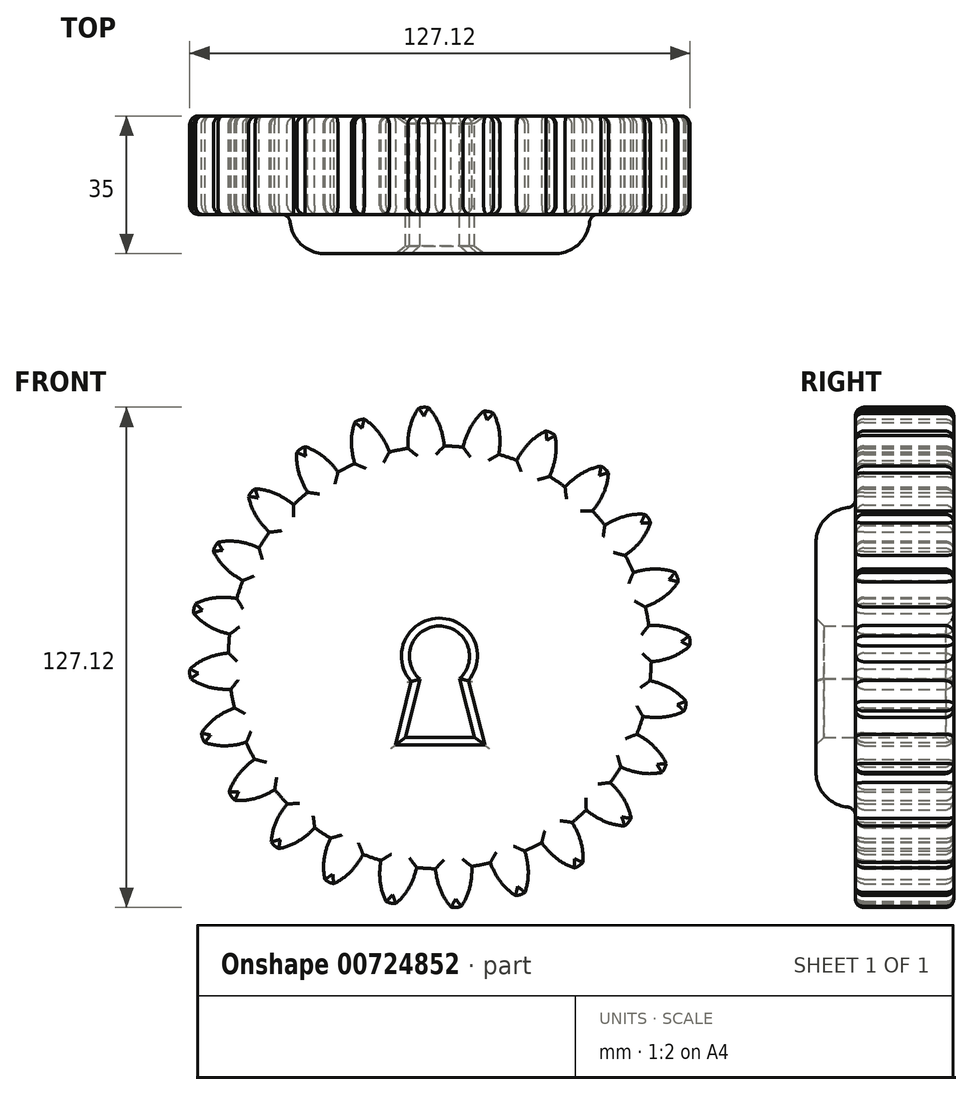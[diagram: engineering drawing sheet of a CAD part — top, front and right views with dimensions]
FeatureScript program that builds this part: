
annotation { "Feature Type Name" : "Feature", "Feature Type Description" : "" }
export const myFeature = defineFeature(function(context is Context, id is Id, definition is map)
    precondition{}
    {
        {
            var Q0;
            Q0=qCreatedBy(makeId("Front.planeOp"),FACE);
            var sketch = newSketch(context, id + "F0", { "sketchPlane" : qUnion([Q0])});
            skCircle(sketch, "E0", {"center": v(0, 0) * mm, "radius": 53.72 * mm});
            skCircle(sketch, "E1", {"center": v(0, 0) * mm, "radius": 58.67 * mm, "construction": true});
            skCircle(sketch, "E2", {"center": v(0, 0) * mm, "radius": 63.5 * mm, "construction": true});
            skLineSegment(sketch, "E3", {"start": v(0, 0) * mm, "end": v(0, 91.84) * mm, "construction": true});
            skLineSegment(sketch, "E4", {"start": v(0, 0) * mm, "end": v(-7.41, 113.09) * mm, "construction": true});
            skLineSegment(sketch, "E5", {"start": v(0, 58.67) * mm, "end": v(-83.5, 56.59) * mm, "construction": true});
            skLineSegment(sketch, "E6", {"start": v(0, 58.67) * mm, "end": v(-75.39, 29.08) * mm, "construction": true});
            skCircle(sketch, "E7", {"center": v(0, 0) * mm, "radius": 54.62 * mm, "construction": true});
            skCircle(sketch, "E8", {"center": v(0, 58.67) * mm, "radius": 16.52 * mm, "construction": true});
            skCircle(sketch, "E9", {"center": v(-15.38, 52.64) * mm, "radius": 16.52 * mm, "construction": true});
            skArc(sketch, "E10", {"start": v(0, 58.67) * mm, "mid": v(-1.21, 61.19) * mm, "end": v(-2.87, 63.43) * mm});
            skArc(sketch, "E11", {"start": v(1.1, 53.7) * mm, "mid": v(0.72, 56.23) * mm, "end": v(0, 58.67) * mm});
            skArc(sketch, "E12.MirrorCS", {"start": v(-8.1, 53.1) * mm, "mid": v(-8.06, 55.65) * mm, "end": v(-7.66, 58.17) * mm});
            skArc(sketch, "E13.MirrorCS", {"start": v(-7.66, 58.17) * mm, "mid": v(-6.78, 60.82) * mm, "end": v(-5.43, 63.27) * mm});
            skArc(sketch, "E14", {"start": v(-2.87, 63.43) * mm, "mid": v(-4.17, 63.55) * mm, "end": v(-5.43, 63.27) * mm});
            skCircle(sketch, "E15", {"center": v(-0.1, 0.31) * mm, "radius": 7.65 * mm});
            skLineSegment(sketch, "E16", {"start": v(-5.08, -5.5) * mm, "end": v(-8.74, -20.3) * mm});
            skLineSegment(sketch, "E17", {"start": v(-8.74, -20.3) * mm, "end": v(8.86, -20.3) * mm});
            skLineSegment(sketch, "E18", {"start": v(8.86, -20.3) * mm, "end": v(5.03, -5.36) * mm});
            skCircle(sketch, "E19", {"center": v(0, 0) * mm, "radius": 38.01 * mm});
            skSolve(sketch);
        }
        {
            var Q0;
            Q0=makeQuery(id+"F0.imprint","IMPRINT",FACE,{"disambiguationData":[TD([[makeQuery(id+"F0.imprint","IMPRINT",EDGE,{"derivedFrom":sQuery(id+"F0.wireOp",EDGE,"E19")}),-1.0]])]});
            var Q1;
            Q1=makeQuery(id+"F0.imprint","IMPRINT",FACE,{"disambiguationData":[TD([[makeQuery(id+"F0.imprint","IMPRINT",EDGE,{"derivedFrom":sQuery(id+"F0.wireOp",EDGE,"E10")}),1.0]])]});
            extrude(context, id + "F1", {"entities" : qUnion([Q0, Q1]), "depth" : 25 * mm, "offsetDistance" : 25 * mm});
        }
        {
            var Q0;
            Q0=makeQuery(id+"F1.opExtrude","SWEPT_BODY",BODY,{"disambiguationData":[OSD([sQuery(id+"F0.wireOp",EDGE,"E0"),sQuery(id+"F0.wireOp",EDGE,"E10"),sQuery(id+"F0.wireOp",EDGE,"E11"),sQuery(id+"F0.wireOp",EDGE,"E12.MirrorCS"),sQuery(id+"F0.wireOp",EDGE,"E13.MirrorCS"),sQuery(id+"F0.wireOp",EDGE,"E14")])]});
            var Q1;
            Q1=makeQuery(id+"F1.opExtrude","SWEPT_FACE",FACE,{"disambiguationData":[OSD([sQuery(id+"F0.wireOp",EDGE,"E0")])]});
            circularPattern(context, id + "F2", {"entities" : qUnion([Q0]), "axis" : qUnion([Q1]), "angle" : 360 * degree, "instanceCount" : 24, "equalSpace" : true});
        }
        {
            var Q0;
            {var subQ1=sQuery(id+"F0.wireOp",EDGE,"E16");Q0=makeQuery(id+"F0.imprint","IMPRINT",FACE,{"disambiguationData":[TD([[makeQuery(id+"F0.imprint","IMPRINT",EDGE,{"derivedFrom":subQ1}),-1.0]])]});}
            extrude(context, id + "F3", {"entities" : qUnion([Q0]), "operationType" : NewBodyOperationType.ADD, "depth" : 35 * mm, "offsetDistance" : 25 * mm});
        }
        {
            var Q0;
            {var subQ0=makeQuery(id+"F1.opExtrude","CAP_FACE",FACE,{"disambiguationData":[OSD([sQuery(id+"F0.wireOp",EDGE,"E0"),sQuery(id+"F0.wireOp",EDGE,"E10"),sQuery(id+"F0.wireOp",EDGE,"E11"),sQuery(id+"F0.wireOp",EDGE,"E12.MirrorCS"),sQuery(id+"F0.wireOp",EDGE,"E13.MirrorCS"),sQuery(id+"F0.wireOp",EDGE,"E14"),sQuery(id+"F0.wireOp",EDGE,"E19")])],"isStart":false});Q0=makeQuery(id+"F3.boolean.opBoolean","MERGE",FACE,{"derivedFrom":[subQ0,makeQuery(id+"F2.opPattern","COPY",FACE,{"derivedFrom":subQ0,"instanceName":"1"}),makeQuery(id+"F2.opPattern","COPY",FACE,{"derivedFrom":subQ0,"instanceName":"2"}),makeQuery(id+"F2.opPattern","COPY",FACE,{"derivedFrom":subQ0,"instanceName":"3"}),makeQuery(id+"F2.opPattern","COPY",FACE,{"derivedFrom":subQ0,"instanceName":"4"}),makeQuery(id+"F2.opPattern","COPY",FACE,{"derivedFrom":subQ0,"instanceName":"5"}),makeQuery(id+"F2.opPattern","COPY",FACE,{"derivedFrom":subQ0,"instanceName":"6"}),makeQuery(id+"F2.opPattern","COPY",FACE,{"derivedFrom":subQ0,"instanceName":"7"}),makeQuery(id+"F2.opPattern","COPY",FACE,{"derivedFrom":subQ0,"instanceName":"8"}),makeQuery(id+"F2.opPattern","COPY",FACE,{"derivedFrom":subQ0,"instanceName":"9"}),makeQuery(id+"F2.opPattern","COPY",FACE,{"derivedFrom":subQ0,"instanceName":"10"}),makeQuery(id+"F2.opPattern","COPY",FACE,{"derivedFrom":subQ0,"instanceName":"11"}),makeQuery(id+"F2.opPattern","COPY",FACE,{"derivedFrom":subQ0,"instanceName":"12"}),makeQuery(id+"F2.opPattern","COPY",FACE,{"derivedFrom":subQ0,"instanceName":"13"}),makeQuery(id+"F2.opPattern","COPY",FACE,{"derivedFrom":subQ0,"instanceName":"14"}),makeQuery(id+"F2.opPattern","COPY",FACE,{"derivedFrom":subQ0,"instanceName":"15"}),makeQuery(id+"F2.opPattern","COPY",FACE,{"derivedFrom":subQ0,"instanceName":"16"}),makeQuery(id+"F2.opPattern","COPY",FACE,{"derivedFrom":subQ0,"instanceName":"17"}),makeQuery(id+"F2.opPattern","COPY",FACE,{"derivedFrom":subQ0,"instanceName":"18"}),makeQuery(id+"F2.opPattern","COPY",FACE,{"derivedFrom":subQ0,"instanceName":"19"}),makeQuery(id+"F2.opPattern","COPY",FACE,{"derivedFrom":subQ0,"instanceName":"20"}),makeQuery(id+"F2.opPattern","COPY",FACE,{"derivedFrom":subQ0,"instanceName":"21"}),makeQuery(id+"F2.opPattern","COPY",FACE,{"derivedFrom":subQ0,"instanceName":"22"}),makeQuery(id+"F2.opPattern","COPY",FACE,{"derivedFrom":subQ0,"instanceName":"23"})]});}
            fillet(context, id + "F4", {"entities" : qUnion([Q0]), "radius" : 2.2 * mm, "tangentPropagation" : true, "allowEdgeOverflow" : false});
        }
        {
            var Q0;
            Q0=makeQuery(id+"F3.opExtrude","CAP_EDGE",EDGE,{"disambiguationData":[OSD([sQuery(id+"F0.wireOp",EDGE,"E19")])],"isStart":false});
            fillet(context, id + "F5", {"entities" : qUnion([Q0]), "radius" : 8.93 * mm, "tangentPropagation" : true, "allowEdgeOverflow" : false});
        }
        {
            var Q0;
            Q0=makeQuery(id+"F3.opExtrude","CAP_EDGE",EDGE,{"disambiguationData":[OSD([sQuery(id+"F0.wireOp",EDGE,"E15")])],"isStart":false});
            var Q1;
            Q1=makeQuery(id+"F3.opExtrude","CAP_EDGE",EDGE,{"disambiguationData":[OSD([sQuery(id+"F0.wireOp",EDGE,"E16")])],"isStart":false});
            var Q2;
            Q2=makeQuery(id+"F3.opExtrude","CAP_EDGE",EDGE,{"disambiguationData":[OSD([sQuery(id+"F0.wireOp",EDGE,"E17")])],"isStart":false});
            var Q3;
            Q3=makeQuery(id+"F3.opExtrude","CAP_EDGE",EDGE,{"disambiguationData":[OSD([sQuery(id+"F0.wireOp",EDGE,"E18")])],"isStart":false});
            var Q4;
            Q4=makeQuery(id+"F3.opExtrude","CAP_EDGE",EDGE,{"disambiguationData":[OSD([sQuery(id+"F0.wireOp",EDGE,"E15")])],"isStart":true});
            var Q5;
            Q5=makeQuery(id+"F3.opExtrude","CAP_EDGE",EDGE,{"disambiguationData":[OSD([sQuery(id+"F0.wireOp",EDGE,"E17")])],"isStart":true});
            var Q6;
            Q6=makeQuery(id+"F3.opExtrude","CAP_EDGE",EDGE,{"disambiguationData":[OSD([sQuery(id+"F0.wireOp",EDGE,"E16")])],"isStart":true});
            var Q7;
            Q7=makeQuery(id+"F3.opExtrude","CAP_EDGE",EDGE,{"disambiguationData":[OSD([sQuery(id+"F0.wireOp",EDGE,"E18")])],"isStart":true});
            chamfer(context, id + "F6", {"entities" : qUnion([Q0, Q1, Q2, Q3, Q4, Q5, Q6, Q7]), "width" : 2 * mm, "tangentPropagation" : true});
        }
        {
            var Q0;
            {var subQ0=sQuery(id+"F0.wireOp",EDGE,"E19");var subQ1=makeQuery(id+"F1.opExtrude","CAP_FACE",FACE,{"disambiguationData":[OSD([sQuery(id+"F0.wireOp",EDGE,"E0"),sQuery(id+"F0.wireOp",EDGE,"E10"),sQuery(id+"F0.wireOp",EDGE,"E11"),sQuery(id+"F0.wireOp",EDGE,"E12.MirrorCS"),sQuery(id+"F0.wireOp",EDGE,"E13.MirrorCS"),sQuery(id+"F0.wireOp",EDGE,"E14"),subQ0])],"isStart":true});Q0=makeQuery(id+"F3.boolean.opBoolean","MERGE",FACE,{"derivedFrom":[subQ1,makeQuery(id+"F2.opPattern","COPY",FACE,{"derivedFrom":subQ1,"instanceName":"1"}),makeQuery(id+"F2.opPattern","COPY",FACE,{"derivedFrom":subQ1,"instanceName":"2"}),makeQuery(id+"F2.opPattern","COPY",FACE,{"derivedFrom":subQ1,"instanceName":"3"}),makeQuery(id+"F2.opPattern","COPY",FACE,{"derivedFrom":subQ1,"instanceName":"4"}),makeQuery(id+"F2.opPattern","COPY",FACE,{"derivedFrom":subQ1,"instanceName":"5"}),makeQuery(id+"F2.opPattern","COPY",FACE,{"derivedFrom":subQ1,"instanceName":"6"}),makeQuery(id+"F2.opPattern","COPY",FACE,{"derivedFrom":subQ1,"instanceName":"7"}),makeQuery(id+"F2.opPattern","COPY",FACE,{"derivedFrom":subQ1,"instanceName":"8"}),makeQuery(id+"F2.opPattern","COPY",FACE,{"derivedFrom":subQ1,"instanceName":"9"}),makeQuery(id+"F2.opPattern","COPY",FACE,{"derivedFrom":subQ1,"instanceName":"10"}),makeQuery(id+"F2.opPattern","COPY",FACE,{"derivedFrom":subQ1,"instanceName":"11"}),makeQuery(id+"F2.opPattern","COPY",FACE,{"derivedFrom":subQ1,"instanceName":"12"}),makeQuery(id+"F2.opPattern","COPY",FACE,{"derivedFrom":subQ1,"instanceName":"13"}),makeQuery(id+"F2.opPattern","COPY",FACE,{"derivedFrom":subQ1,"instanceName":"14"}),makeQuery(id+"F2.opPattern","COPY",FACE,{"derivedFrom":subQ1,"instanceName":"15"}),makeQuery(id+"F2.opPattern","COPY",FACE,{"derivedFrom":subQ1,"instanceName":"16"}),makeQuery(id+"F2.opPattern","COPY",FACE,{"derivedFrom":subQ1,"instanceName":"17"}),makeQuery(id+"F2.opPattern","COPY",FACE,{"derivedFrom":subQ1,"instanceName":"18"}),makeQuery(id+"F2.opPattern","COPY",FACE,{"derivedFrom":subQ1,"instanceName":"19"}),makeQuery(id+"F2.opPattern","COPY",FACE,{"derivedFrom":subQ1,"instanceName":"20"}),makeQuery(id+"F2.opPattern","COPY",FACE,{"derivedFrom":subQ1,"instanceName":"21"}),makeQuery(id+"F2.opPattern","COPY",FACE,{"derivedFrom":subQ1,"instanceName":"22"}),makeQuery(id+"F2.opPattern","COPY",FACE,{"derivedFrom":subQ1,"instanceName":"23"}),makeQuery(id+"F3.opExtrude","CAP_FACE",FACE,{"disambiguationData":[OSD([sQuery(id+"F0.wireOp",EDGE,"E15"),sQuery(id+"F0.wireOp",EDGE,"E16"),sQuery(id+"F0.wireOp",EDGE,"E17"),sQuery(id+"F0.wireOp",EDGE,"E18"),subQ0])],"isStart":true})]});}
            fillet(context, id + "F7", {"entities" : qUnion([Q0]), "radius" : 2.2 * mm, "tangentPropagation" : true, "allowEdgeOverflow" : false});
        }
    });
